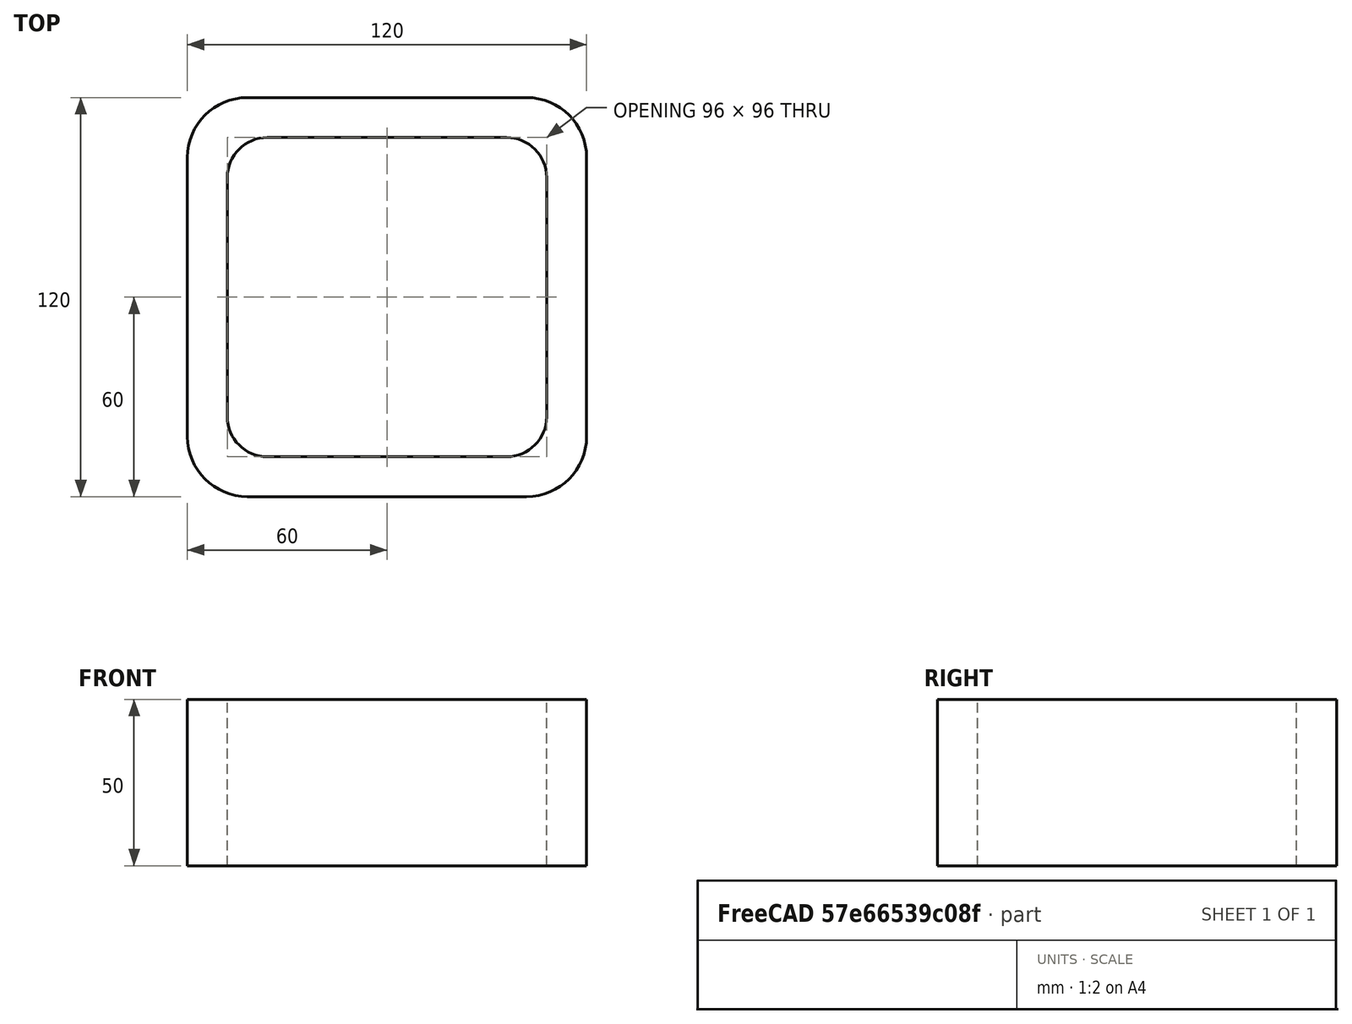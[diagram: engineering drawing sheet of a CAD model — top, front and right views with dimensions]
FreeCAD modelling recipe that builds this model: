
FCSTD DOCUMENT  (FreeCAD 0.15R4671 (Git))
Label: Square hollow section 120x120x12 EN10219 S235JRH
License: All rights reserved
LicenseURL: http://en.wikipedia.org/wiki/All_rights_reserved
objects: Sketcher::SketchObject×1, Part::Extrusion×1
note: 2 computed .brp shape members not serialized (recipe doc carries the construction recipe); baked Part::Feature solids carry a one-line shape summary decoded from their .brp

FEATURE [Sketcher::SketchObject] Sketch
  sketch-geometry (16):
    g0: LineSegment StartX=-36 StartY=48 StartZ=0 EndX=36 EndY=48 EndZ=0
    g1: LineSegment StartX=48 StartY=36 StartZ=0 EndX=48 EndY=-36 EndZ=0
    g2: LineSegment StartX=36 StartY=-48 StartZ=0 EndX=-36 EndY=-48 EndZ=0
    g3: LineSegment StartX=-48 StartY=-36 StartZ=0 EndX=-48 EndY=36 EndZ=0
    g4: LineSegment StartX=-42 StartY=60 StartZ=0 EndX=42 EndY=60 EndZ=0
    g5: LineSegment StartX=60 StartY=42 StartZ=0 EndX=60 EndY=-42 EndZ=0
    g6: LineSegment StartX=42 StartY=-60 StartZ=0 EndX=-42 EndY=-60 EndZ=0
    g7: LineSegment StartX=-60 StartY=-42 StartZ=0 EndX=-60 EndY=42 EndZ=0
    g8: ArcOfCircle CenterX=-36 CenterY=36 CenterZ=0 NormalX=0 NormalY=0 NormalZ=1 Radius=12 StartAngle=1.5708 EndAngle=3.14159
    g9: ArcOfCircle CenterX=36 CenterY=36 CenterZ=0 NormalX=0 NormalY=0 NormalZ=1 Radius=12 StartAngle=0 EndAngle=1.5708
    g10: ArcOfCircle CenterX=36 CenterY=-36 CenterZ=0 NormalX=0 NormalY=0 NormalZ=1 Radius=12 StartAngle=4.71239 EndAngle=6.28319
    g11: ArcOfCircle CenterX=-36 CenterY=-36 CenterZ=0 NormalX=0 NormalY=0 NormalZ=1 Radius=12 StartAngle=3.14159 EndAngle=4.71239
    g12: ArcOfCircle CenterX=42 CenterY=42 CenterZ=0 NormalX=0 NormalY=0 NormalZ=1 Radius=18 StartAngle=0 EndAngle=1.5708
    g13: ArcOfCircle CenterX=42 CenterY=-42 CenterZ=0 NormalX=0 NormalY=0 NormalZ=1 Radius=18 StartAngle=4.71239 EndAngle=6.28319
    g14: ArcOfCircle CenterX=-42 CenterY=-42 CenterZ=0 NormalX=0 NormalY=0 NormalZ=1 Radius=18 StartAngle=3.14159 EndAngle=4.71239
    g15: ArcOfCircle CenterX=-42 CenterY=42 CenterZ=0 NormalX=0 NormalY=0 NormalZ=1 Radius=18 StartAngle=1.5708 EndAngle=3.14159
  constraints (36):
    c: Horizontal(g2)
    c: Vertical(g3)
    c: Horizontal(g6)
    c: Vertical(g7)
    c: Tangent(g3,g8) = 1.5708
    c: Tangent(g0,g8) = 1.5708
    c: Tangent(g0,g9) = 1.5708
    c: Tangent(g1,g9) = 1.5708
    c: Tangent(g1,g10) = 1.5708
    c: Tangent(g2,g10) = 1.5708
    c: Tangent(g2,g11) = 1.5708
    c: Tangent(g3,g11) = 1.5708
    c: Tangent(g4,g12) = 1.5708
    c: Tangent(g5,g12) = 1.5708
    c: Tangent(g5,g13) = 1.5708
    c: Tangent(g6,g13) = 1.5708
    c: Tangent(g6,g14) = 1.5708
    c: Tangent(g7,g14) = 1.5708
    c: Tangent(g7,g15) = 1.5708
    c: Tangent(g4,g15) = 1.5708
    c: Equal(g9,g8)
    c: Equal(g9,g11)
    c: Equal(g9,g10)
    c: Equal(g12,g15)
    c: Equal(g12,g14)
    c: Equal(g12,g13)
    c: Symmetric(g4,g6,g-1)
    c: Symmetric(g7,g5,g-2)
    c: DistanceY(g4,g6) = -120
    c: DistanceX(g7,g5) = 120
    c: Symmetric(g3,g1,g-2)
    c: Symmetric(g0,g2,g-1)
    c: DistanceY(g0,g4) = 12
    c: DistanceX(g5,g1) = -12
    c: Radius(g9) = 12
    c: Radius(g12) = 18
FEATURE [Part::Extrusion] Extrude  label="Square hollow section 120x120x12 EN10219 S235JRH"
  Base = -> Sketch
  Dir = (0,0,50)
  Solid = true
